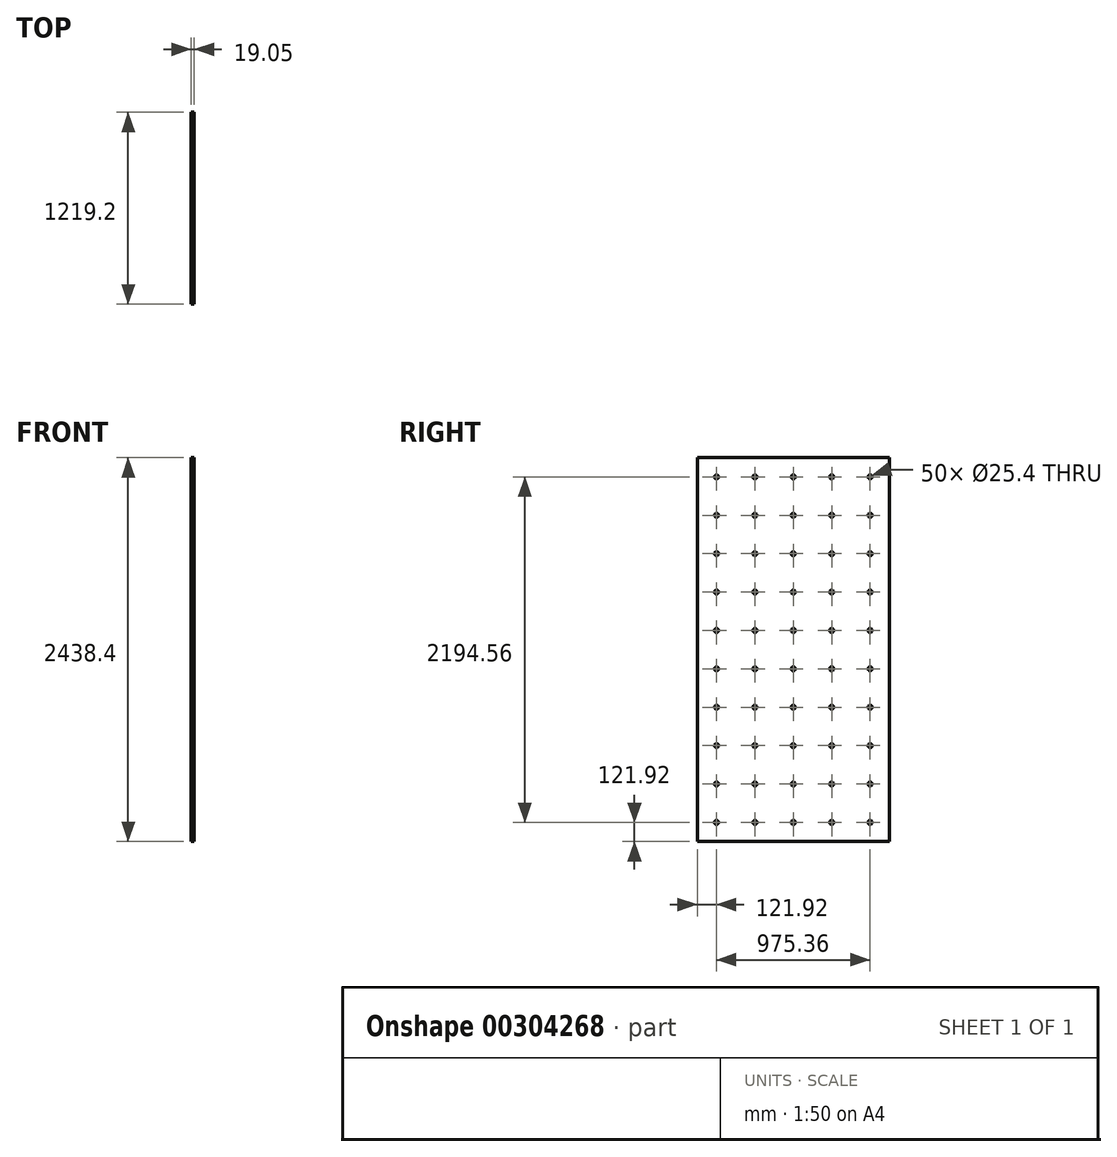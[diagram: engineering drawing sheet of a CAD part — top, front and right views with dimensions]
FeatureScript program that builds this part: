
annotation { "Feature Type Name" : "Feature", "Feature Type Description" : "" }
export const myFeature = defineFeature(function(context is Context, id is Id, definition is map)
    precondition{}
    {
        {
            var Q0;
            Q0=qCreatedBy(makeId("Right.planeOp"),FACE);
            var sketch = newSketch(context, id + "F0", { "sketchPlane" : qUnion([Q0])});
            skLineSegment(sketch, "E0.bottom", {"start": v(0, 0) * mm, "end": v(1219.2, 0) * mm});
            skLineSegment(sketch, "E0.top", {"start": v(0, 2438.4) * mm, "end": v(1219.2, 2438.4) * mm});
            skLineSegment(sketch, "E0.left", {"start": v(0, 0) * mm, "end": v(0, 2438.4) * mm});
            skLineSegment(sketch, "E0.right", {"start": v(1219.2, 0) * mm, "end": v(1219.2, 2438.4) * mm});
            skPoint(sketch, "E0.middle", {"position": v(609.6, 1219.2) * mm});
            skSolve(sketch);
        }
        {
            var Q0;
            Q0 = qSketchRegion(id + "F0", true);
            extrude(context, id + "F1", {"entities" : qUnion([Q0]), "depth" : 19.05 * mm});
        }
        {
            var Q0;
            Q0=makeQuery(id+"F1.opExtrude","CAP_FACE",FACE,{"disambiguationData":[OSD([sQuery(id+"F0.wireOp",EDGE,"E0.bottom"),sQuery(id+"F0.wireOp",EDGE,"E0.top"),sQuery(id+"F0.wireOp",EDGE,"E0.left"),sQuery(id+"F0.wireOp",EDGE,"E0.right")])],"isStart":true});
            var sketch = newSketch(context, id + "F2", { "sketchPlane" : qUnion([Q0])});
            skCircle(sketch, "E1", {"center": v(-1097.28, 2316.48) * mm, "radius": 12.7 * mm});
            skCircle(sketch, "E2.0.1.0", {"center": v(-1097.28, 2072.64) * mm, "radius": 12.7 * mm});
            skCircle(sketch, "E2.0.2.0", {"center": v(-1097.28, 1828.8) * mm, "radius": 12.7 * mm});
            skCircle(sketch, "E2.0.3.0", {"center": v(-1097.28, 1584.96) * mm, "radius": 12.7 * mm});
            skCircle(sketch, "E2.0.4.0", {"center": v(-1097.28, 1341.12) * mm, "radius": 12.7 * mm});
            skCircle(sketch, "E2.0.5.0", {"center": v(-1097.28, 1097.28) * mm, "radius": 12.7 * mm});
            skCircle(sketch, "E2.0.6.0", {"center": v(-1097.28, 853.44) * mm, "radius": 12.7 * mm});
            skCircle(sketch, "E2.1.0.0", {"center": v(-853.44, 2316.48) * mm, "radius": 12.7 * mm});
            skCircle(sketch, "E2.1.1.0", {"center": v(-853.44, 2072.64) * mm, "radius": 12.7 * mm});
            skCircle(sketch, "E2.1.2.0", {"center": v(-853.44, 1828.8) * mm, "radius": 12.7 * mm});
            skCircle(sketch, "E2.1.3.0", {"center": v(-853.44, 1584.96) * mm, "radius": 12.7 * mm});
            skCircle(sketch, "E2.1.4.0", {"center": v(-853.44, 1341.12) * mm, "radius": 12.7 * mm});
            skCircle(sketch, "E2.1.5.0", {"center": v(-853.44, 1097.28) * mm, "radius": 12.7 * mm});
            skCircle(sketch, "E2.1.6.0", {"center": v(-853.44, 853.44) * mm, "radius": 12.7 * mm});
            skCircle(sketch, "E2.2.0.0", {"center": v(-609.6, 2316.48) * mm, "radius": 12.7 * mm});
            skCircle(sketch, "E2.2.1.0", {"center": v(-609.6, 2072.64) * mm, "radius": 12.7 * mm});
            skCircle(sketch, "E2.2.2.0", {"center": v(-609.6, 1828.8) * mm, "radius": 12.7 * mm});
            skCircle(sketch, "E2.2.3.0", {"center": v(-609.6, 1584.96) * mm, "radius": 12.7 * mm});
            skCircle(sketch, "E2.2.4.0", {"center": v(-609.6, 1341.12) * mm, "radius": 12.7 * mm});
            skCircle(sketch, "E2.2.5.0", {"center": v(-609.6, 1097.28) * mm, "radius": 12.7 * mm});
            skCircle(sketch, "E2.2.6.0", {"center": v(-609.6, 853.44) * mm, "radius": 12.7 * mm});
            skLineSegment(sketch, "E2.direction1", {"start": v(-1097.28, 2316.48) * mm, "end": v(-853.44, 2316.48) * mm, "construction": true});
            skLineSegment(sketch, "E2.direction2", {"start": v(-1097.28, 2316.48) * mm, "end": v(-1097.28, 2072.64) * mm, "construction": true});
            skLineSegment(sketch, "E3", {"start": v(-1097.28, 2316.48) * mm, "end": v(-1219.2, 2316.48) * mm, "construction": true});
            skLineSegment(sketch, "E4", {"start": v(-1097.28, 2316.48) * mm, "end": v(-1097.28, 2438.4) * mm, "construction": true});
            skLineSegment(sketch, "E5", {"start": v(-975.36, 2316.48) * mm, "end": v(-975.36, 2194.56) * mm, "construction": true});
            skLineSegment(sketch, "E6", {"start": v(-975.36, 2194.56) * mm, "end": v(-1097.28, 2194.56) * mm, "construction": true});
            skCircle(sketch, "E7.0.3.0", {"center": v(-365.76, 2316.48) * mm, "radius": 12.7 * mm});
            skCircle(sketch, "E7.0.3.1", {"center": v(-365.76, 2072.64) * mm, "radius": 12.7 * mm});
            skCircle(sketch, "E7.0.3.2", {"center": v(-365.76, 1828.8) * mm, "radius": 12.7 * mm});
            skCircle(sketch, "E7.0.3.3", {"center": v(-365.76, 1584.96) * mm, "radius": 12.7 * mm});
            skCircle(sketch, "E7.0.3.4", {"center": v(-365.76, 1341.12) * mm, "radius": 12.7 * mm});
            skCircle(sketch, "E7.0.3.5", {"center": v(-365.76, 1097.28) * mm, "radius": 12.7 * mm});
            skCircle(sketch, "E7.0.3.6", {"center": v(-365.76, 853.44) * mm, "radius": 12.7 * mm});
            skCircle(sketch, "E8.0.0.7", {"center": v(-1097.28, 609.6) * mm, "radius": 12.7 * mm});
            skCircle(sketch, "E8.0.1.7", {"center": v(-853.44, 609.6) * mm, "radius": 12.7 * mm});
            skCircle(sketch, "E8.0.2.7", {"center": v(-609.6, 609.6) * mm, "radius": 12.7 * mm});
            skCircle(sketch, "E8.0.3.7", {"center": v(-365.76, 609.6) * mm, "radius": 12.7 * mm});
            skCircle(sketch, "E9.0.4.0", {"center": v(-121.92, 2316.48) * mm, "radius": 12.7 * mm});
            skCircle(sketch, "E9.0.4.1", {"center": v(-121.92, 2072.64) * mm, "radius": 12.7 * mm});
            skCircle(sketch, "E9.0.4.2", {"center": v(-121.92, 1828.8) * mm, "radius": 12.7 * mm});
            skCircle(sketch, "E9.0.4.3", {"center": v(-121.92, 1584.96) * mm, "radius": 12.7 * mm});
            skCircle(sketch, "E9.0.4.4", {"center": v(-121.92, 1341.12) * mm, "radius": 12.7 * mm});
            skCircle(sketch, "E9.0.4.5", {"center": v(-121.92, 1097.28) * mm, "radius": 12.7 * mm});
            skCircle(sketch, "E9.0.4.6", {"center": v(-121.92, 853.44) * mm, "radius": 12.7 * mm});
            skCircle(sketch, "E9.0.4.7", {"center": v(-121.92, 609.6) * mm, "radius": 12.7 * mm});
            skCircle(sketch, "E10.0.0.8", {"center": v(-1097.28, 365.76) * mm, "radius": 12.7 * mm});
            skCircle(sketch, "E10.0.0.9", {"center": v(-1097.28, 121.92) * mm, "radius": 12.7 * mm});
            skCircle(sketch, "E10.0.1.8", {"center": v(-853.44, 365.76) * mm, "radius": 12.7 * mm});
            skCircle(sketch, "E10.0.1.9", {"center": v(-853.44, 121.92) * mm, "radius": 12.7 * mm});
            skCircle(sketch, "E10.0.2.8", {"center": v(-609.6, 365.76) * mm, "radius": 12.7 * mm});
            skCircle(sketch, "E10.0.2.9", {"center": v(-609.6, 121.92) * mm, "radius": 12.7 * mm});
            skCircle(sketch, "E10.0.3.8", {"center": v(-365.76, 365.76) * mm, "radius": 12.7 * mm});
            skCircle(sketch, "E10.0.3.9", {"center": v(-365.76, 121.92) * mm, "radius": 12.7 * mm});
            skCircle(sketch, "E10.0.4.8", {"center": v(-121.92, 365.76) * mm, "radius": 12.7 * mm});
            skCircle(sketch, "E10.0.4.9", {"center": v(-121.92, 121.92) * mm, "radius": 12.7 * mm});
            skLineSegment(sketch, "E11", {"start": v(-121.92, 2316.48) * mm, "end": v(0, 2316.48) * mm, "construction": true});
            skLineSegment(sketch, "E12", {"start": v(-1097.28, 121.92) * mm, "end": v(-1097.28, 0) * mm, "construction": true});
            skSolve(sketch);
        }
        {
            var Q0;
            Q0 = qSketchRegion(id + "F2", true);
            extrude(context, id + "F3", {"entities" : qUnion([Q0]), "operationType" : NewBodyOperationType.REMOVE, "depth" : 381 * mm, "hasSecondDirection" : true, "secondDirectionOppositeDirection" : true, "secondDirectionDepth" : 25.4 * mm});
        }
    });
